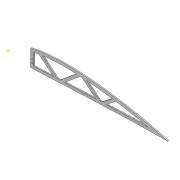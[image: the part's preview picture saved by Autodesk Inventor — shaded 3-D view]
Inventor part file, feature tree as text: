
AUTODESK INVENTOR PART (.ipt)
format: ipt  version: 2022 (Build 260153000, 153)  size: 322,048 bytes
history: native  units: mm
features: sketch x8, extrude x7, projected_geometry x4, shell x1
ambient origin geometry x8: Origin, YZ Plane, XZ Plane, XY Plane, X Axis, Y Axis, Z Axis, Center Point
bodies: Solid1 (feature_tree)
feature tree (20):
  extrude  "Extrusion1"  Depth=5.0mm
  shell  "Shell1"  Thickness=6.0mm
  extrude  "Extrusion2"  Depth=2.0mm
  extrude  "Extrusion3"  Depth=5.9mm
  extrude  "Extrusion4"  Depth=10.0mm TaperAngle=0.0deg
  extrude  "Extrusion5"  Depth=10.0mm TaperAngle=0.0deg
  extrude  "Extrusion7"  Depth=5.0mm
  sketch  "Sketch15"  dims[d20=5.0mm d21=5.0mm]
  sketch  "Sketch16"  dims[d22=4.5mm d23=0.0mm d24=2.0mm d26=2.0mm d29=4.5mm d30=0.0mm d31=2.5mm d32=0.0mm]
  extrude  "Extrusion8"  Depth=5.0mm
  sketch  "Sketch3"  dims[d0=4.5mm d1=0.0mm d2=5.0mm d3=6.0mm]
  sketch  "Sketch7"  dims[d5=4.5mm d6=0.0mm d7=2.0mm]
  projected_geometry  "Projected Loop3"
  sketch  "Sketch8"  dims[d8=2.0mm d9=5.9mm]
  sketch  "Sketch9"  dims[d12=4.0mm d13=10.0mm d14=0.0mm]
  sketch  "Sketch10"  dims[d15=40.0mm d16=10.0mm d17=0.0mm]
  projected_geometry  "Projected Loop4"
  sketch  "Sketch14"  dims[d18=5.0mm d19=5.0mm]
  projected_geometry  "Projected Loop7"
  projected_geometry  "Projected Loop8"
